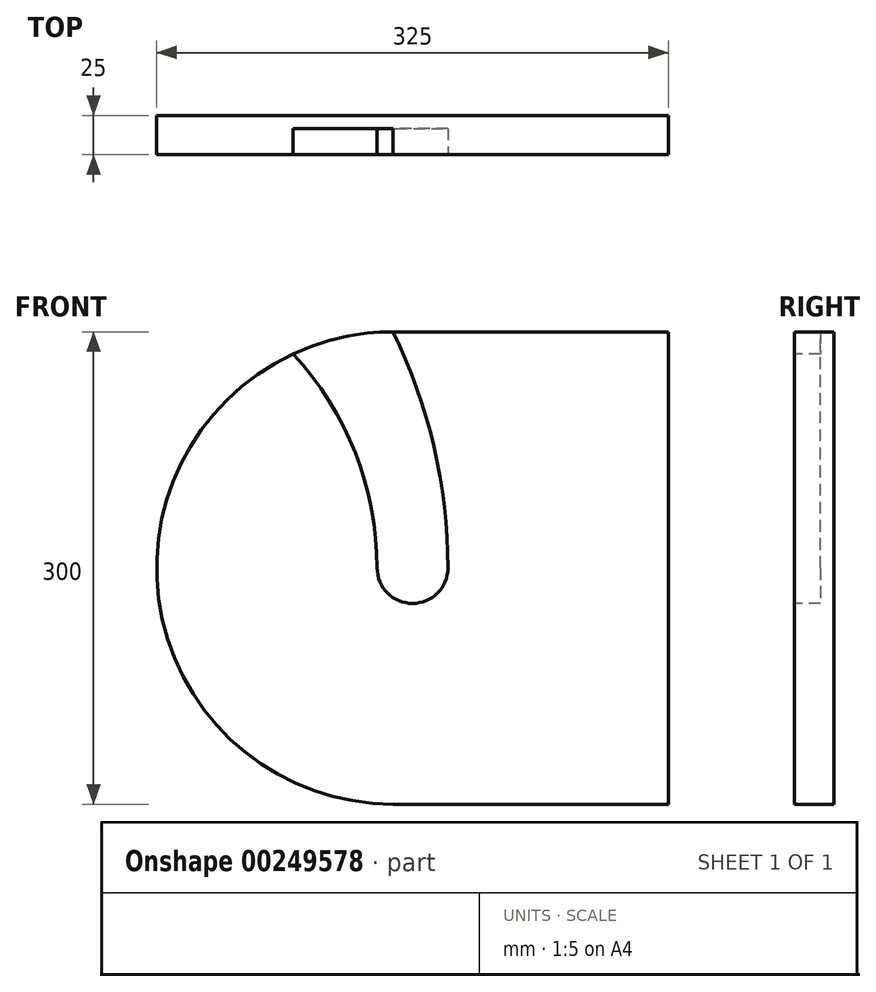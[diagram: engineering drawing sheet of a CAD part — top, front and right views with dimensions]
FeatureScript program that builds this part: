
annotation { "Feature Type Name" : "Feature", "Feature Type Description" : "" }
export const myFeature = defineFeature(function(context is Context, id is Id, definition is map)
    precondition{}
    {
        {
            assignVariable(context, id + "F0", {"name" : "Thickness", "anyValue" : 25});
        }
        {
            assignVariable(context, id + "F1", {"name" : "PaperWidth", "anyValue" : 350});
        }
        {
            var Q0;
            Q0=qCreatedBy(makeId("Front.planeOp"),FACE);
            var sketch = newSketch(context, id + "F2", { "sketchPlane" : qUnion([Q0])});
            skLineSegment(sketch, "E0.bottom", {"start": v(-12.5, 150) * mm, "end": v(162.5, 150) * mm});
            skLineSegment(sketch, "E0.top", {"start": v(-12.5, -150) * mm, "end": v(162.5, -150) * mm});
            skLineSegment(sketch, "E0.left", {"start": v(-162.5, 0) * mm, "end": v(-162.5, 0) * mm});
            skLineSegment(sketch, "E0.right", {"start": v(162.5, 150) * mm, "end": v(162.5, -150) * mm});
            skLineSegment(sketch, "E1", {"start": v(0, 150) * mm, "end": v(0, -150) * mm, "construction": true});
            skPoint(sketch, "E2", {"position": v(0, 0) * mm});
            skArc(sketch, "E3", {"start": v(-22.5, 0) * mm, "mid": v(0, -22.5) * mm, "end": v(22.5, 0) * mm});
            skPoint(sketch, "E4.visualSharp", {"position": v(-162.5, 150) * mm});
            skArc(sketch, "E4.filletArc", {"start": v(-12.5, 150) * mm, "mid": v(-118.57, 106.07) * mm, "end": v(-162.5, 0) * mm});
            skPoint(sketch, "E5.visualSharp", {"position": v(-162.5, -150) * mm});
            skArc(sketch, "E5.filletArc", {"start": v(-162.5, 0) * mm, "mid": v(-118.57, -106.07) * mm, "end": v(-12.5, -150) * mm});
            skArc(sketch, "E6", {"start": v(22.5, 0) * mm, "mid": v(13.63, 77.01) * mm, "end": v(-12.5, 150) * mm});
            skArc(sketch, "E7", {"start": v(-22.5, 0) * mm, "mid": v(-36.32, 73.03) * mm, "end": v(-75.88, 135.95) * mm});
            skSolve(sketch);
        }
        {
            var Q0;
            Q0=makeQuery(id+"F2.imprint","IMPRINT",FACE,{"disambiguationData":[TD([[makeQuery(id+"F2.imprint","IMPRINT",EDGE,{"derivedFrom":sQuery(id+"F2.wireOp",EDGE,"E0.bottom")}),-1.0]])]});
            var Q1;
            Q1=makeQuery(id+"F2.imprint","IMPRINT",FACE,{"disambiguationData":[TD([[makeQuery(id+"F2.imprint","IMPRINT",EDGE,{"derivedFrom":sQuery(id+"F2.wireOp",EDGE,"E3")}),1.0]])]});
            extrude(context, id + "F3", {"entities" : qUnion([Q0, Q1]), "oppositeDirection" : true, "depth" : (getVariable(context, 'Thickness')) * mm});
        }
        {
            var Q0;
            Q0=makeQuery(id+"F2.imprint","IMPRINT",FACE,{"disambiguationData":[TD([[makeQuery(id+"F2.imprint","IMPRINT",EDGE,{"derivedFrom":sQuery(id+"F2.wireOp",EDGE,"E3")}),1.0]])]});
            extrude(context, id + "F4", {"entities" : qUnion([Q0]), "operationType" : NewBodyOperationType.REMOVE, "oppositeDirection" : true, "depth" : (getVariable(context, 'Thickness') * 2 / 3) * mm});
        }
        {
            var Q0;
            Q0=makeQuery(id+"F3.opExtrude","CAP_FACE",FACE,{"disambiguationData":[OSD([sQuery(id+"F2.wireOp",EDGE,"E0.bottom"),sQuery(id+"F2.wireOp",EDGE,"E0.top"),sQuery(id+"F2.wireOp",EDGE,"E0.right"),sQuery(id+"F2.wireOp",EDGE,"E4.filletArc"),sQuery(id+"F2.wireOp",EDGE,"E5.filletArc")])],"isStart":false});
            var sketch = newSketch(context, id + "F5", { "sketchPlane" : qUnion([Q0])});
            skLineSegment(sketch, "E8.bottom", {"start": v(-162.5, 150) * mm, "end": v(-137.5, 150) * mm});
            skLineSegment(sketch, "E8.top", {"start": v(-162.5, -150) * mm, "end": v(-137.5, -150) * mm});
            skLineSegment(sketch, "E8.left", {"start": v(-162.5, 150) * mm, "end": v(-162.5, -150) * mm});
            skLineSegment(sketch, "E8.right", {"start": v(-137.5, 150) * mm, "end": v(-137.5, -150) * mm});
            skSolve(sketch);
        }
        {
            var Q0;
            Q0=qSketchRegion(id+"F5",true);
            extrude(context, id + "F6", {"entities" : qUnion([Q0]), "oppositeDirection" : true, "depth" : (getVariable(context, 'PaperWidth') + (getVariable(context, 'Thickness') * 2)) * mm});
        }
        {
            var Q0;
            Q0=makeQuery(id+"F6.opExtrude","SWEPT_EDGE",EDGE,{"disambiguationData":[OSD([sQuery(id+"F2.wireOp",EDGE,"E0.bottom"),sQuery(id+"F5.wireOp",EDGE,"E8.bottom"),sQuery(id+"F5.wireOp",EDGE,"E8.right")])]});
            cPoint(context, id + "F7", {"entities" : qUnion([Q0]), "parameter" : 0.5});
        }
        {
            var Q0;
            Q0=makeQuery(id+"F6.opExtrude","CAP_FACE",FACE,{"disambiguationData":[OSD([sQuery(id+"F5.wireOp",EDGE,"E8.bottom"),sQuery(id+"F5.wireOp",EDGE,"E8.top"),sQuery(id+"F5.wireOp",EDGE,"E8.left"),sQuery(id+"F5.wireOp",EDGE,"E8.right")])],"isStart":false});
            var Q1;
            Q1=qCreatedBy(id+"F7",VERTEX);
            cPlane(context, id + "F8", {"entities" : qUnion([Q0, Q1]), "cplaneType" : CPlaneType.PLANE_POINT, "offset" : 25 * mm, "width" : 150 * mm, "height" : 150 * mm});
        }
        {
            var Q0;
            Q0=makeQuery(id+"F3.opExtrude","SWEPT_BODY",BODY,{"disambiguationData":[OSD([sQuery(id+"F2.wireOp",EDGE,"E0.bottom"),sQuery(id+"F2.wireOp",EDGE,"E0.top"),sQuery(id+"F2.wireOp",EDGE,"E0.right"),sQuery(id+"F2.wireOp",EDGE,"E4.filletArc"),sQuery(id+"F2.wireOp",EDGE,"E5.filletArc")])]});
            var Q1;
            Q1=qCreatedBy(id+"F8.planeOp",FACE);
            mirror(context, id + "F9", {"entities" : qUnion([Q0]), "mirrorPlane" : qUnion([Q1])});
        }
        {
            var Q0;
            Q0=makeQuery(id+"F3.opExtrude","SWEPT_BODY",BODY,{"disambiguationData":[OSD([sQuery(id+"F2.wireOp",EDGE,"E0.bottom"),sQuery(id+"F2.wireOp",EDGE,"E0.top"),sQuery(id+"F2.wireOp",EDGE,"E0.right"),sQuery(id+"F2.wireOp",EDGE,"E4.filletArc"),sQuery(id+"F2.wireOp",EDGE,"E5.filletArc")])]});
            transform(context, id + "F10", {"entities" : qUnion([Q0]), "transformType" : TransformType.TRANSLATION_3D, "dx" : 0 * mm, "dy" : 0 * mm, "dz" : 0 * mm, "makeCopy" : true});
        }
        {
            var Q0;
            Q0=makeQuery(id+"F10.opPattern","COPY",BODY,{"derivedFrom":makeQuery(id+"F3.opExtrude","SWEPT_BODY",BODY,{"disambiguationData":[OSD([sQuery(id+"F2.wireOp",EDGE,"E0.bottom"),sQuery(id+"F2.wireOp",EDGE,"E0.top"),sQuery(id+"F2.wireOp",EDGE,"E0.right"),sQuery(id+"F2.wireOp",EDGE,"E4.filletArc"),sQuery(id+"F2.wireOp",EDGE,"E5.filletArc")])]}),"instanceName":"1"});
            deleteBodies(context, id + "F11", {"entities" : qUnion([Q0])});
        }
        {
            var Q0;
            Q0=makeQuery(id+"F9.opPattern","COPY",BODY,{"derivedFrom":makeQuery(id+"F3.opExtrude","SWEPT_BODY",BODY,{"disambiguationData":[OSD([sQuery(id+"F2.wireOp",EDGE,"E0.bottom"),sQuery(id+"F2.wireOp",EDGE,"E0.top"),sQuery(id+"F2.wireOp",EDGE,"E0.right"),sQuery(id+"F2.wireOp",EDGE,"E4.filletArc"),sQuery(id+"F2.wireOp",EDGE,"E5.filletArc")])]}),"instanceName":"1"});
            deleteBodies(context, id + "F12", {"entities" : qUnion([Q0])});
        }
        {
            var Q0;
            Q0=makeQuery(id+"F6.opExtrude","SWEPT_BODY",BODY,{"disambiguationData":[OSD([sQuery(id+"F5.wireOp",EDGE,"E8.bottom"),sQuery(id+"F5.wireOp",EDGE,"E8.top"),sQuery(id+"F5.wireOp",EDGE,"E8.left"),sQuery(id+"F5.wireOp",EDGE,"E8.right")])]});
            deleteBodies(context, id + "F13", {"entities" : qUnion([Q0])});
        }
    });
